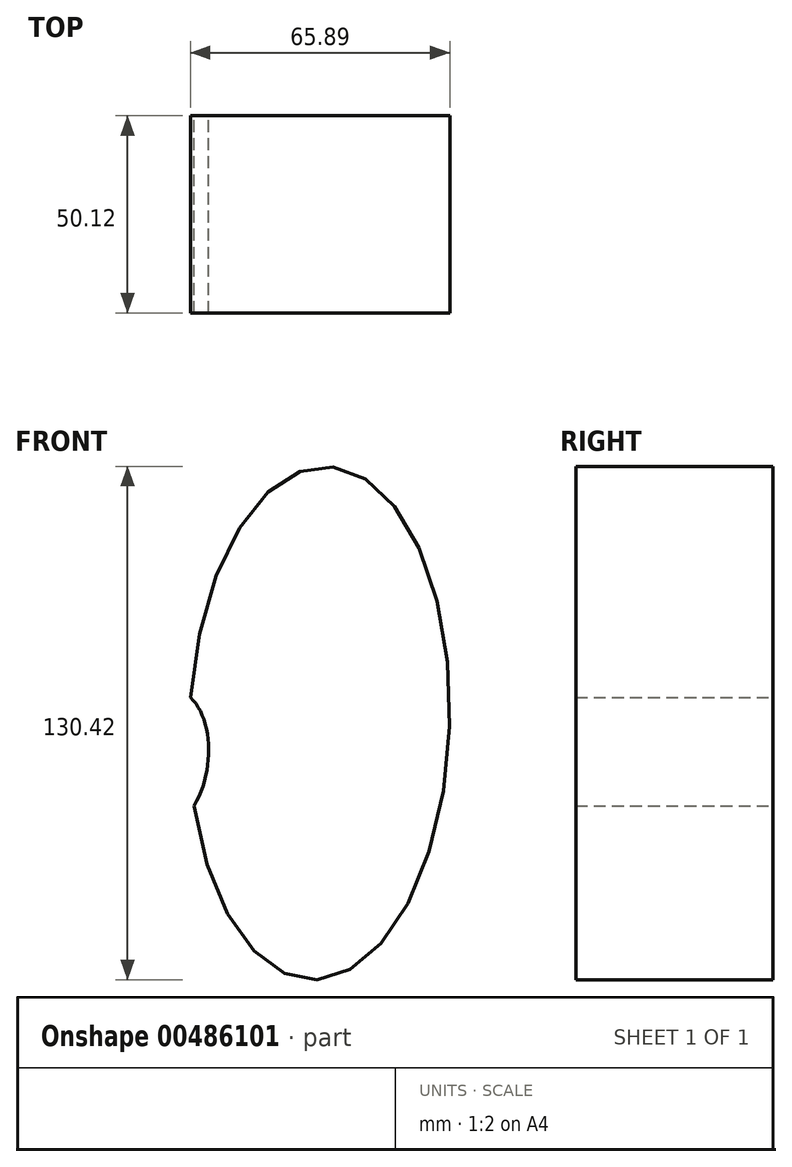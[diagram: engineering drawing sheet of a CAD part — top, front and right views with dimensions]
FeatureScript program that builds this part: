
annotation { "Feature Type Name" : "Feature", "Feature Type Description" : "" }
export const myFeature = defineFeature(function(context is Context, id is Id, definition is map)
    precondition{}
    {
        {
            var Q0;
            Q0=qCreatedBy(makeId("Front.planeOp"),FACE);
            var sketch = newSketch(context, id + "F0", { "sketchPlane" : qUnion([Q0])});
            skFitSpline(sketch, "E0", {"points": [v(0, 0) * mm, v(-36.33, 6.04) * mm, v(0, 35.06) * mm, v(0, 0) * mm]});
            skSolve(sketch);
        }
        {
            var Q0;
            Q0 = qSketchRegion(id + "F0", true);
            var sketch = newSketch(context, id + "F1", { "sketchPlane" : qUnion([Q0])});
            skEllipse(sketch, "E1", {"center": v(36.28, 26.32) * mm, "majorRadius": 65.23 * mm, "minorRadius": 33.08 * mm, "majorAxis": v(-0.03, -1)});
            skSolve(sketch);
        }
        {
            var Q0;
            {var subQ0=sQuery(id+"F1.wireOp",EDGE,"E1");var subQ1=makeQuery(id+"F0.imprint","IMPRINT",EDGE,{"derivedFrom":sQuery(id+"F0.wireOp",EDGE,"E0")});var subQ2=makeQuery(id+"F1.imprint","INTERSECT",VERTEX,{"disambiguationData":[OD(0.0)],"derivedFrom":[subQ1,subQ0]});Q0=makeQuery(id+"F1.imprint","IMPRINT",FACE,{"disambiguationData":[TD([[makeQuery(id+"F1.imprint","IMPRINT",EDGE,{"disambiguationData":[TD([[subQ2,-1.0]])],"derivedFrom":subQ0}),1.0]])]});}
            extrude(context, id + "F2", {"entities" : qUnion([Q0]), "depth" : 50.12 * mm});
        }
    });
